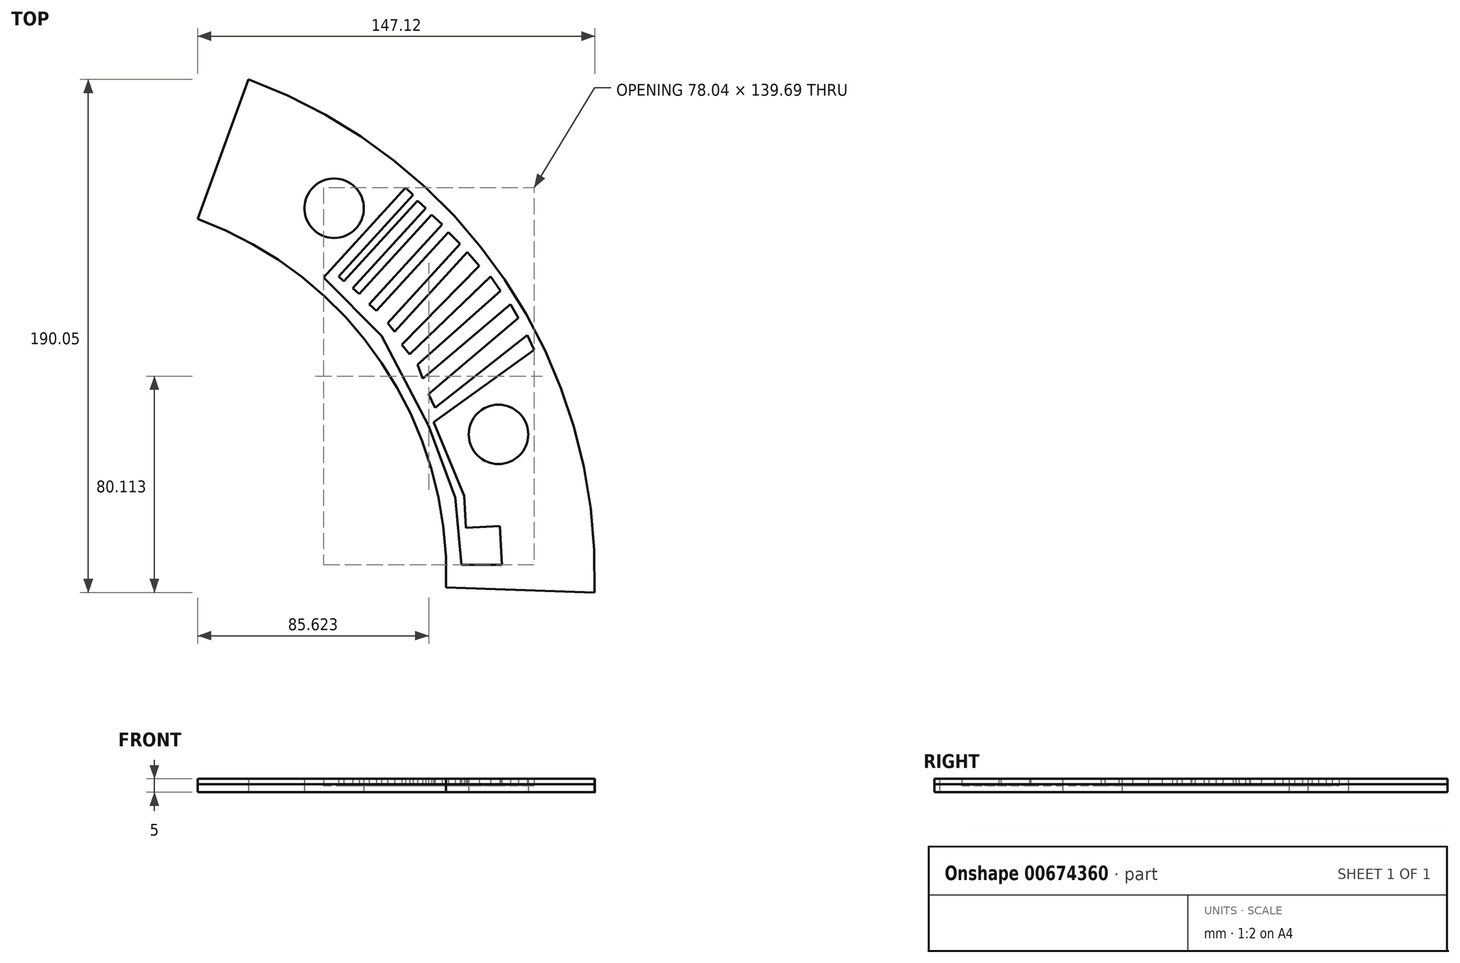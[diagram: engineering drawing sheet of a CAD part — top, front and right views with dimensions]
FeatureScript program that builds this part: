
annotation { "Feature Type Name" : "Feature", "Feature Type Description" : "" }
export const myFeature = defineFeature(function(context is Context, id is Id, definition is map)
    precondition{}
    {
        {
            var Q0;
            Q0=qCreatedBy(makeId("Top.planeOp"),FACE);
            var sketch = newSketch(context, id + "F0", { "sketchPlane" : qUnion([Q0])});
            skCircle(sketch, "E0", {"center": v(0, 0) * mm, "radius": 195 * mm});
            skLineSegment(sketch, "E1", {"start": v(-236.95, 0) * mm, "end": v(264.25, 0) * mm, "construction": true});
            skLineSegment(sketch, "E2", {"start": v(0, -228.62) * mm, "end": v(0, 236.65) * mm, "construction": true});
            skCircle(sketch, "E3", {"center": v(0, 0) * mm, "radius": 140 * mm});
            skCircle(sketch, "E4", {"center": v(0, 0) * mm, "radius": 167.5 * mm});
            skPoint(sketch, "E5", {"position": v(0, 167.5) * mm});
            skPoint(sketch, "E6.1.0", {"position": v(-98.45, 135.51) * mm});
            skPoint(sketch, "E6.2.0", {"position": v(-159.3, 51.76) * mm});
            skPoint(sketch, "E6.3.0", {"position": v(-159.3, -51.76) * mm});
            skPoint(sketch, "E6.4.0", {"position": v(-98.45, -135.51) * mm});
            skPoint(sketch, "E6.5.0", {"position": v(0, -167.5) * mm});
            skPoint(sketch, "E6.6.0", {"position": v(98.45, -135.51) * mm});
            skPoint(sketch, "E6.7.0", {"position": v(159.3, -51.76) * mm});
            skPoint(sketch, "E6.8.0", {"position": v(159.3, 51.76) * mm});
            skPoint(sketch, "E6.9.0", {"position": v(98.45, 135.51) * mm});
            skLineSegment(sketch, "E7", {"start": v(0, 0) * mm, "end": v(91.1, 250.3) * mm});
            skLineSegment(sketch, "E8", {"start": v(0, 0) * mm, "end": v(-87.39, -240.1) * mm});
            skLineSegment(sketch, "E9", {"start": v(0, 0) * mm, "end": v(-255.48, 8.92) * mm});
            skLineSegment(sketch, "E10", {"start": v(0, 0) * mm, "end": v(300.02, -10.48) * mm});
            skSolve(sketch);
        }
        {
            var Q0;
            {var subQ0=sQuery(id+"F0.wireOp",EDGE,"E7");var subQ1=sQuery(id+"F0.wireOp",EDGE,"E3");var subQ2=makeQuery(id+"F0.imprint","INTERSECT",VERTEX,{"derivedFrom":[subQ1,subQ0]});Q0=makeQuery(id+"F0.imprint","IMPRINT",FACE,{"disambiguationData":[TD([[makeQuery(id+"F0.imprint","IMPRINT",EDGE,{"disambiguationData":[TD([[subQ2,1.0]])],"derivedFrom":subQ1}),-1.0]])]});}
            var Q1;
            {var subQ0=sQuery(id+"F0.wireOp",EDGE,"E7");var subQ1=sQuery(id+"F0.wireOp",EDGE,"E0");var subQ2=makeQuery(id+"F0.imprint","INTERSECT",VERTEX,{"derivedFrom":[subQ1,subQ0]});Q1=makeQuery(id+"F0.imprint","IMPRINT",FACE,{"disambiguationData":[TD([[makeQuery(id+"F0.imprint","IMPRINT",EDGE,{"disambiguationData":[TD([[subQ2,1.0]])],"derivedFrom":subQ1}),1.0]])]});}
            extrude(context, id + "F1", {"entities" : qUnion([Q0, Q1]), "depth" : 3 * mm, "offsetDistance" : 25 * mm});
        }
        {
            var Q0;
            Q0=sQuery(id+"F0.wireOp",VERTEX,"E6.9.0");
            var Q1;
            Q1=sQuery(id+"F0.wireOp",VERTEX,"E6.8.0");
            var Q2;
            Q2=sQuery(id+"F0.wireOp",VERTEX,"E6.7.0");
            var Q3;
            Q3=makeQuery(id+"F1.opExtrude","SWEPT_BODY",BODY,{"disambiguationData":[OSD([sQuery(id+"F0.wireOp",EDGE,"E0"),sQuery(id+"F0.wireOp",EDGE,"E3"),sQuery(id+"F0.wireOp",EDGE,"E7"),sQuery(id+"F0.wireOp",EDGE,"7779584a-14d0-4c0c-a12f-be6d3e54e7f4.3.0")])]});
            hole(context, id + "F2", {"style" : HoleStyle.SIMPLE, "endStyle" : HoleEndStyle.THROUGH, "oppositeDirection" : true, "standardTappedOrClearance" : lookupTablePath({ "standard" : "ISO", "size" : "22", "type" : "Drilled" }), "standardBlindInLast" : lookupTablePath({ "standard" : "ISO", "size" : "22", "type" : "Drilled" }), "holeDiameter" : 22 * mm, "majorDiameter" : 5 * mm, "tappedDepth" : 30 * mm, "tapClearance" : 3, "locations" : qUnion([Q0, Q1, Q2]), "scope" : qUnion([Q3])});
        }
        {
            var Q0;
            Q0=makeQuery(id+"F1.opExtrude","CAP_FACE",FACE,{"disambiguationData":[OSD([sQuery(id+"F0.wireOp",EDGE,"E0"),sQuery(id+"F0.wireOp",EDGE,"E3"),sQuery(id+"F0.wireOp",EDGE,"E7"),sQuery(id+"F0.wireOp",EDGE,"E10")])],"isStart":false});
            var sketch = newSketch(context, id + "F3", { "sketchPlane" : qUnion([Q0])});
            skLineSegment(sketch, "E11", {"start": v(94.48, 109.93) * mm, "end": v(124.86, 143.15) * mm});
            skLineSegment(sketch, "E12", {"start": v(124.86, 143.15) * mm, "end": v(127.74, 140.51) * mm});
            skLineSegment(sketch, "E13", {"start": v(127.74, 140.51) * mm, "end": v(100.09, 110.27) * mm});
            skLineSegment(sketch, "E14", {"start": v(100.09, 110.27) * mm, "end": v(102.09, 108.44) * mm});
            skLineSegment(sketch, "E15", {"start": v(102.09, 108.44) * mm, "end": v(129.35, 138.25) * mm});
            skLineSegment(sketch, "E16", {"start": v(129.35, 138.25) * mm, "end": v(132.35, 135.51) * mm});
            skLineSegment(sketch, "E17", {"start": v(132.35, 135.51) * mm, "end": v(105.35, 105.98) * mm});
            skLineSegment(sketch, "E18", {"start": v(105.35, 105.98) * mm, "end": v(107.71, 103.82) * mm});
            skLineSegment(sketch, "E19", {"start": v(107.71, 103.82) * mm, "end": v(134.5, 133.12) * mm});
            skLineSegment(sketch, "E20", {"start": v(134.5, 133.12) * mm, "end": v(138.46, 129.5) * mm});
            skLineSegment(sketch, "E21", {"start": v(138.46, 129.5) * mm, "end": v(111.48, 100) * mm});
            skLineSegment(sketch, "E22", {"start": v(111.48, 100) * mm, "end": v(114.16, 97.55) * mm});
            skLineSegment(sketch, "E23", {"start": v(114.16, 97.55) * mm, "end": v(140.74, 126.62) * mm});
            skLineSegment(sketch, "E24", {"start": v(140.74, 126.62) * mm, "end": v(145.04, 122.26) * mm});
            skLineSegment(sketch, "E25", {"start": v(145.04, 122.26) * mm, "end": v(118.3, 93.02) * mm});
            skLineSegment(sketch, "E26", {"start": v(118.3, 93.02) * mm, "end": v(120.8, 89.77) * mm});
            skLineSegment(sketch, "E27", {"start": v(120.8, 89.77) * mm, "end": v(147.75, 119.25) * mm});
            skLineSegment(sketch, "E28", {"start": v(147.75, 119.25) * mm, "end": v(152.14, 114.22) * mm});
            skLineSegment(sketch, "E29", {"start": v(152.14, 114.22) * mm, "end": v(123.56, 84.9) * mm});
            skLineSegment(sketch, "E30", {"start": v(123.56, 84.9) * mm, "end": v(126.46, 81.38) * mm});
            skLineSegment(sketch, "E31", {"start": v(126.46, 81.38) * mm, "end": v(156.38, 110.27) * mm});
            skLineSegment(sketch, "E32", {"start": v(156.38, 110.27) * mm, "end": v(160.14, 104.9) * mm});
            skLineSegment(sketch, "E33", {"start": v(160.14, 104.9) * mm, "end": v(129.36, 77.63) * mm});
            skLineSegment(sketch, "E34", {"start": v(129.36, 77.63) * mm, "end": v(131.2, 72.45) * mm});
            skLineSegment(sketch, "E35", {"start": v(131.2, 72.45) * mm, "end": v(163.72, 100) * mm});
            skLineSegment(sketch, "E36", {"start": v(163.72, 100) * mm, "end": v(166.65, 94.9) * mm});
            skLineSegment(sketch, "E37", {"start": v(166.65, 94.9) * mm, "end": v(133.35, 66.68) * mm});
            skLineSegment(sketch, "E38", {"start": v(133.35, 66.68) * mm, "end": v(135.84, 61.6) * mm});
            skLineSegment(sketch, "E39", {"start": v(135.84, 61.6) * mm, "end": v(169.93, 88.47) * mm});
            skLineSegment(sketch, "E40", {"start": v(169.93, 88.47) * mm, "end": v(172.52, 83.05) * mm});
            skLineSegment(sketch, "E41", {"start": v(172.52, 83.05) * mm, "end": v(135.24, 56.3) * mm});
            skLineSegment(sketch, "E42", {"start": v(133.35, 54.94) * mm, "end": v(116, 88.24) * mm});
            skLineSegment(sketch, "E43", {"start": v(116, 88.24) * mm, "end": v(94.48, 109.93) * mm});
            skLineSegment(sketch, "E44", {"start": v(133.35, 54.94) * mm, "end": v(143.35, 28.38) * mm});
            skLineSegment(sketch, "E45", {"start": v(143.35, 28.38) * mm, "end": v(145.57, 3.46) * mm});
            skLineSegment(sketch, "E46", {"start": v(145.57, 3.46) * mm, "end": v(160.54, 3.46) * mm});
            skLineSegment(sketch, "E47", {"start": v(160.54, 3.46) * mm, "end": v(159.76, 17.84) * mm});
            skLineSegment(sketch, "E48", {"start": v(159.76, 17.84) * mm, "end": v(147.27, 17.15) * mm});
            skLineSegment(sketch, "E49", {"start": v(147.27, 17.15) * mm, "end": v(146.62, 28.98) * mm});
            skLineSegment(sketch, "E50", {"start": v(146.62, 28.98) * mm, "end": v(135.24, 56.3) * mm});
            skSolve(sketch);
        }
        {
            var Q0;
            Q0=makeQuery(id+"F3.imprint","IMPRINT",FACE,{"disambiguationData":[TD([[makeQuery(id+"F3.imprint","IMPRINT",EDGE,{"derivedFrom":sQuery(id+"F3.wireOp",EDGE,"E11")}),-1.0]])]});
            var Q1;
            Q1=sQuery(id+"F3.wireOp",EDGE,"E34");
            extrude(context, id + "F4", {"entities" : qUnion([Q0]), "operationType" : NewBodyOperationType.REMOVE, "surfaceEntities" : qUnion([Q1]), "oppositeDirection" : true, "depth" : 0.5 * mm, "offsetDistance" : 25 * mm});
        }
        {
            var Q0;
            Q0 = qSketchRegion(id + "F3", true);
            extrude(context, id + "F5", {"entities" : qUnion([Q0]), "oppositeDirection" : true, "depth" : 0.5 * mm, "offsetDistance" : 25 * mm});
        }
        {
            var Q0;
            Q0=makeQuery(id+"F1.opExtrude","CAP_FACE",FACE,{"disambiguationData":[OSD([sQuery(id+"F0.wireOp",EDGE,"E0"),sQuery(id+"F0.wireOp",EDGE,"E3"),sQuery(id+"F0.wireOp",EDGE,"E7"),sQuery(id+"F0.wireOp",EDGE,"E10")])],"isStart":false});
            var sketch = newSketch(context, id + "F6", { "sketchPlane" : qUnion([Q0])});
            skSolve(sketch);
        }
        {
            var Q0;
            Q0 = qSketchRegion(id + "F6", true);
            var Q1;
            {var subQ3=sQuery(id+"F0.wireOp",EDGE,"E0");Q1=makeQuery(id+"F6.imprint","IMPRINT",FACE,{"disambiguationData":[TD([[makeQuery(id+"F6.imprint","IMPRINT",EDGE,{"derivedFrom":makeQuery(id+"F1.opExtrude","CAP_EDGE",EDGE,{"disambiguationData":[OSD([subQ3])],"isStart":false})}),1.0]])]});}
            var Q2;
            Q2=makeQuery(id+"F6.imprint","IMPRINT",FACE,{"disambiguationData":[TD([[makeQuery(id+"F6.imprint","IMPRINT",EDGE,{"derivedFrom":makeQuery(id+"F4.boolean.opBoolean","COPY",EDGE,{"derivedFrom":makeQuery(id+"F4.opExtrude","CAP_EDGE",EDGE,{"disambiguationData":[OSD([sQuery(id+"F3.wireOp",EDGE,"E11")])],"isStart":true})})}),-1.0]])]});
            extrude(context, id + "F7", {"entities" : qUnion([Q0, Q1, Q2]), "depth" : 2 * mm, "offsetDistance" : 25 * mm});
        }
    });
